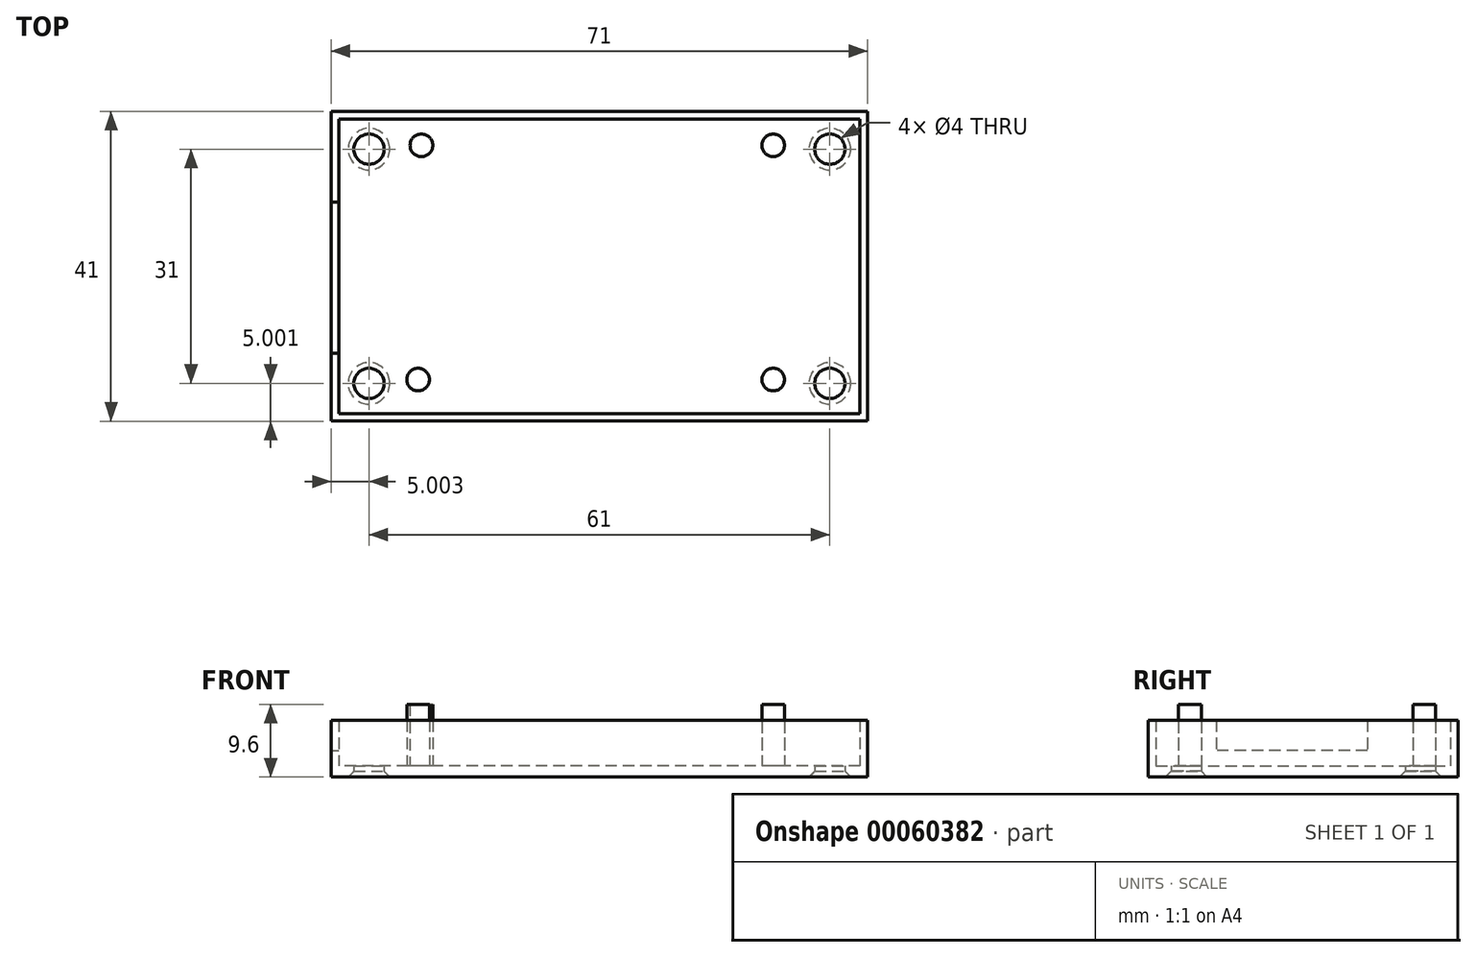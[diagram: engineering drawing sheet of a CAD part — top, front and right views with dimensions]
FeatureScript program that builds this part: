
annotation { "Feature Type Name" : "Feature", "Feature Type Description" : "" }
export const myFeature = defineFeature(function(context is Context, id is Id, definition is map)
    precondition{}
    {
        {
            var Q0;
            Q0=qCreatedBy(makeId("Top.planeOp"),FACE);
            var sketch = newSketch(context, id + "F0", { "sketchPlane" : qUnion([Q0])});
            skLineSegment(sketch, "E0.bottom", {"start": v(-12.76, 68.41) * mm, "end": v(56.24, 68.41) * mm});
            skLineSegment(sketch, "E0.top", {"start": v(-12.76, 29.41) * mm, "end": v(56.24, 29.41) * mm});
            skLineSegment(sketch, "E0.left", {"start": v(-12.76, 68.41) * mm, "end": v(-12.76, 29.41) * mm});
            skLineSegment(sketch, "E0.right", {"start": v(56.24, 68.41) * mm, "end": v(56.24, 29.41) * mm});
            skCircle(sketch, "E1", {"center": v(-8.76, 64.41) * mm, "radius": 1.5 * mm, "construction": true});
            skCircle(sketch, "E2", {"center": v(-8.76, 33.41) * mm, "radius": 1.5 * mm, "construction": true});
            skCircle(sketch, "E3", {"center": v(52.24, 64.41) * mm, "radius": 1.5 * mm, "construction": true});
            skCircle(sketch, "E4", {"center": v(52.24, 33.41) * mm, "radius": 1.5 * mm, "construction": true});
            skCircle(sketch, "E5.0", {"center": v(52.24, 33.41) * mm, "radius": 2 * mm});
            skCircle(sketch, "E6.0", {"center": v(52.24, 64.41) * mm, "radius": 2 * mm});
            skCircle(sketch, "E7.0", {"center": v(-8.76, 64.41) * mm, "radius": 2 * mm});
            skCircle(sketch, "E8.0", {"center": v(-8.76, 33.41) * mm, "radius": 2 * mm});
            skPoint(sketch, "E9", {"position": v(-2.26, 33.91) * mm});
            skLineSegment(sketch, "E10.0", {"start": v(-13.76, 69.41) * mm, "end": v(-13.76, 28.41) * mm});
            skLineSegment(sketch, "E10.1", {"start": v(-13.76, 69.41) * mm, "end": v(57.24, 69.41) * mm});
            skLineSegment(sketch, "E10.2", {"start": v(57.24, 69.41) * mm, "end": v(57.24, 28.41) * mm});
            skLineSegment(sketch, "E10.3", {"start": v(-13.76, 28.41) * mm, "end": v(57.24, 28.41) * mm});
            skPoint(sketch, "E11", {"position": v(-13.76, 57.41) * mm});
            skPoint(sketch, "E12", {"position": v(-13.76, 37.41) * mm});
            skLineSegment(sketch, "E13", {"start": v(-13.76, 57.41) * mm, "end": v(-12.76, 57.41) * mm});
            skLineSegment(sketch, "E14", {"start": v(-13.76, 37.41) * mm, "end": v(-12.76, 37.41) * mm});
            skPoint(sketch, "E15", {"position": v(-1.82, 64.91) * mm});
            skPoint(sketch, "E16", {"position": v(44.74, 33.91) * mm});
            skPoint(sketch, "E17", {"position": v(44.74, 64.91) * mm});
            skCircle(sketch, "E18", {"center": v(-2.26, 33.91) * mm, "radius": 1.5 * mm});
            skCircle(sketch, "E19", {"center": v(-1.82, 64.91) * mm, "radius": 1.5 * mm});
            skCircle(sketch, "E20", {"center": v(44.74, 64.91) * mm, "radius": 1.5 * mm});
            skCircle(sketch, "E21", {"center": v(44.74, 33.91) * mm, "radius": 1.5 * mm});
            skSolve(sketch);
        }
        {
            var Q0;
            {var subQ0=sQuery(id+"F0.wireOp",EDGE,"E0.bottom");Q0=makeQuery(id+"F0.imprint","IMPRINT",FACE,{"disambiguationData":[TD([[makeQuery(id+"F0.imprint","IMPRINT",EDGE,{"derivedFrom":subQ0}),-1.0]])]});}
            var Q1;
            {var subQ5=sQuery(id+"F0.wireOp",EDGE,"E0.bottom");Q1=makeQuery(id+"F0.imprint","IMPRINT",FACE,{"disambiguationData":[TD([[makeQuery(id+"F0.imprint","IMPRINT",EDGE,{"derivedFrom":subQ5}),1.0]])]});}
            var Q2;
            Q2=makeQuery(id+"F0.imprint","IMPRINT",FACE,{"disambiguationData":[TD([[makeQuery(id+"F0.imprint","IMPRINT",EDGE,{"derivedFrom":sQuery(id+"F0.wireOp",EDGE,"E18")}),1.0]])]});
            var Q3;
            Q3=makeQuery(id+"F0.imprint","IMPRINT",FACE,{"disambiguationData":[TD([[makeQuery(id+"F0.imprint","IMPRINT",EDGE,{"derivedFrom":sQuery(id+"F0.wireOp",EDGE,"E21")}),1.0]])]});
            var Q4;
            Q4=makeQuery(id+"F0.imprint","IMPRINT",FACE,{"disambiguationData":[TD([[makeQuery(id+"F0.imprint","IMPRINT",EDGE,{"derivedFrom":sQuery(id+"F0.wireOp",EDGE,"E20")}),1.0]])]});
            var Q5;
            Q5=makeQuery(id+"F0.imprint","IMPRINT",FACE,{"disambiguationData":[TD([[makeQuery(id+"F0.imprint","IMPRINT",EDGE,{"derivedFrom":sQuery(id+"F0.wireOp",EDGE,"E19")}),1.0]])]});
            var Q6;
            {var subQ0=sQuery(id+"F0.wireOp",EDGE,"E13");Q6=makeQuery(id+"F0.imprint","IMPRINT",FACE,{"disambiguationData":[TD([[makeQuery(id+"F0.imprint","IMPRINT",EDGE,{"derivedFrom":subQ0}),-1.0]])]});}
            extrude(context, id + "F1", {"entities" : qUnion([Q0, Q1, Q2, Q3, Q4, Q5, Q6]), "depth" : 1.5 * mm});
        }
        {
            var Q0;
            {var subQ5=sQuery(id+"F0.wireOp",EDGE,"E0.bottom");Q0=makeQuery(id+"F0.imprint","IMPRINT",FACE,{"disambiguationData":[TD([[makeQuery(id+"F0.imprint","IMPRINT",EDGE,{"derivedFrom":subQ5}),1.0]])]});}
            extrude(context, id + "F2", {"entities" : qUnion([Q0]), "operationType" : NewBodyOperationType.ADD, "depth" : 7.5 * mm});
        }
        {
            var Q0;
            Q0=makeQuery(id+"F0.imprint","IMPRINT",FACE,{"disambiguationData":[TD([[makeQuery(id+"F0.imprint","IMPRINT",EDGE,{"derivedFrom":sQuery(id+"F0.wireOp",EDGE,"E19")}),1.0]])]});
            var Q1;
            Q1=makeQuery(id+"F0.imprint","IMPRINT",FACE,{"disambiguationData":[TD([[makeQuery(id+"F0.imprint","IMPRINT",EDGE,{"derivedFrom":sQuery(id+"F0.wireOp",EDGE,"E18")}),1.0]])]});
            var Q2;
            Q2=makeQuery(id+"F0.imprint","IMPRINT",FACE,{"disambiguationData":[TD([[makeQuery(id+"F0.imprint","IMPRINT",EDGE,{"derivedFrom":sQuery(id+"F0.wireOp",EDGE,"E21")}),1.0]])]});
            var Q3;
            Q3=makeQuery(id+"F0.imprint","IMPRINT",FACE,{"disambiguationData":[TD([[makeQuery(id+"F0.imprint","IMPRINT",EDGE,{"derivedFrom":sQuery(id+"F0.wireOp",EDGE,"E20")}),1.0]])]});
            extrude(context, id + "F3", {"entities" : qUnion([Q0, Q1, Q2, Q3]), "operationType" : NewBodyOperationType.ADD, "depth" : 9.6 * mm});
        }
        {
            var Q0;
            {var subQ0=sQuery(id+"F0.wireOp",EDGE,"E13");Q0=makeQuery(id+"F0.imprint","IMPRINT",FACE,{"disambiguationData":[TD([[makeQuery(id+"F0.imprint","IMPRINT",EDGE,{"derivedFrom":subQ0}),-1.0]])]});}
            extrude(context, id + "F4", {"entities" : qUnion([Q0]), "operationType" : NewBodyOperationType.ADD, "depth" : 3.5 * mm});
        }
        {
            var Q0;
            Q0=sQuery(id+"F0.wireOp",VERTEX,"E3.center");
            var Q1;
            Q1=sQuery(id+"F0.wireOp",VERTEX,"E4.center");
            var Q2;
            Q2=sQuery(id+"F0.wireOp",VERTEX,"E2.center");
            var Q3;
            Q3=sQuery(id+"F0.wireOp",VERTEX,"E1.center");
            var Q4;
            Q4=makeQuery(id+"F1.opExtrude","SWEPT_BODY",BODY,{"disambiguationData":[OSD([sQuery(id+"F0.wireOp",EDGE,"E5.0"),sQuery(id+"F0.wireOp",EDGE,"E6.0"),sQuery(id+"F0.wireOp",EDGE,"E7.0"),sQuery(id+"F0.wireOp",EDGE,"E8.0"),sQuery(id+"F0.wireOp",EDGE,"E10.0"),sQuery(id+"F0.wireOp",EDGE,"E10.1"),sQuery(id+"F0.wireOp",EDGE,"E10.2"),sQuery(id+"F0.wireOp",EDGE,"E10.3")])]});
            hole(context, id + "F5", {"style" : HoleStyle.C_SINK, "holeDiameter" : 3 * mm, "cSinkDiameter" : 5.5 * mm, "endStyle" : HoleEndStyle.THROUGH, "oppositeDirection" : true, "locations" : qUnion([Q0, Q1, Q2, Q3]), "scope" : qUnion([Q4]), "cSinkAngle" : 90 * degree});
        }
    });
